# Revit family: MI-G-SS
name_source: partatom
category: Pipe Accessories
revit_build: Autodesk Revit 2018 (Build: 20170223_1515(x64)
units: mm (PartAtom-declared; Revit-internal decimal feet)

## family parameters
Always vertical = Yes
Cut with Voids When Loaded = No
Part Type = Normal
Round Connector Dimension = Use Diameter
Shared = No
Work Plane-Based = No

## types (8) — shared parameters
Description = 4 TO 50 G.P.M. STAINLESS STEEL GREASE INTERCEPTOR
Manufacturer = MIFAB
Model = MI-G-SS
URL = WWW.MIFAB.COM

## per-type parameters (varying)
| type | A-Width | B-Length | C-Pipe Offset | E-Height | F |
| MI-G-0-SS | 17 " | 11 " | 3 " | 11 " | 2 " |
| MI-G-1-SS | 18 " | 14 " | 4 " | 12 " | 2 " |
| MI-G-2-SS | 21 " | 16 " | 4 " | 13 " | 2 " |
| MI-G-3-SS | 24 " | 16 " | 4 " | 15 " | 2 " |
| MI-G-4-SS | 24 " | 16 " | 4 " | 18 " | 3 " |
| MI-G-5-SS | 28 " | 19 " | 4 " | 18 " | 3 " |
| MI-G-6-SS | 31 " | 24 " | 6 " | 22 " | 3 " |
| MI-G-7-SS | 31 " | 24 " | 6 " | 24 " | 3 " |

## geometry (parser evidence)
native form markers: Sweep x5
no freeform markers — native parametric forms only
